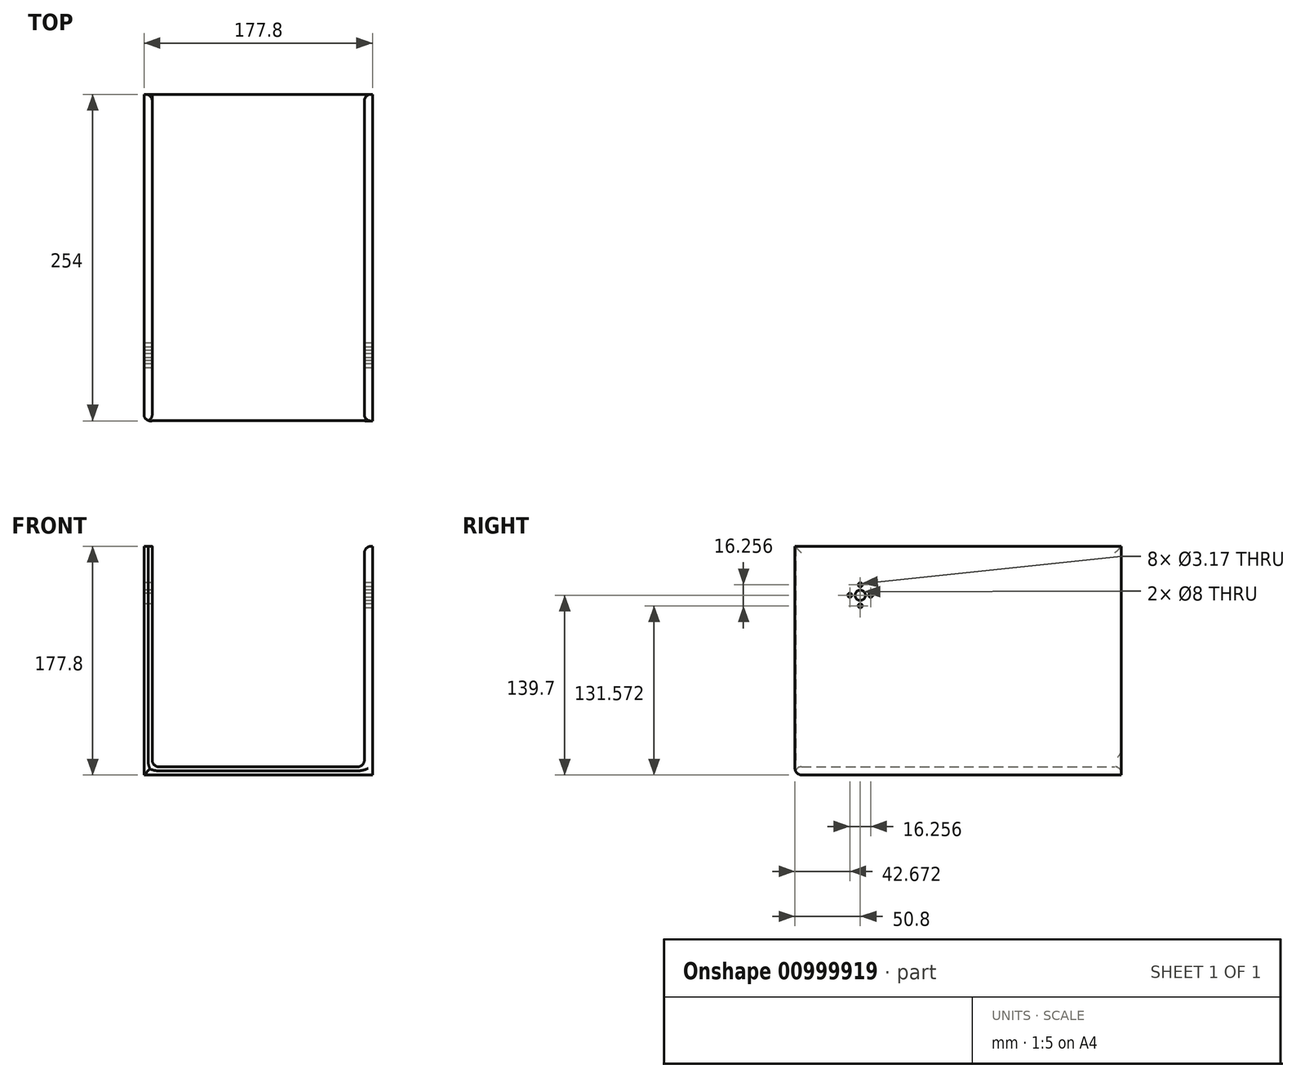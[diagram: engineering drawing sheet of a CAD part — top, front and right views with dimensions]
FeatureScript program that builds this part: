
annotation { "Feature Type Name" : "Feature", "Feature Type Description" : "" }
export const myFeature = defineFeature(function(context is Context, id is Id, definition is map)
    precondition{}
    {
        {
            var Q0;
            Q0=qCreatedBy(makeId("Front.planeOp"),FACE);
            var sketch = newSketch(context, id + "F0", { "sketchPlane" : qUnion([Q0])});
            skLineSegment(sketch, "E0.bottom", {"start": v(88.9, -88.9) * mm, "end": v(-88.9, -88.9) * mm});
            skLineSegment(sketch, "E0.top", {"start": v(88.9, 88.9) * mm, "end": v(82.55, 88.9) * mm});
            skLineSegment(sketch, "E0.left", {"start": v(88.9, -88.9) * mm, "end": v(88.9, 88.9) * mm});
            skLineSegment(sketch, "E0.right", {"start": v(-88.9, -88.9) * mm, "end": v(-88.9, 88.9) * mm});
            skPoint(sketch, "E0.middle", {"position": v(0, 0) * mm});
            skLineSegment(sketch, "E1.top", {"start": v(82.55, -82.55) * mm, "end": v(-82.55, -82.55) * mm});
            skPoint(sketch, "E1.right.start.orphan", {"position": v(-82.55, 82.55) * mm});
            skPoint(sketch, "E1.left.start.orphan", {"position": v(82.55, 82.55) * mm});
            skLineSegment(sketch, "E2", {"start": v(-82.55, -82.55) * mm, "end": v(-82.55, 88.9) * mm});
            skLineSegment(sketch, "E3", {"start": v(82.55, -82.55) * mm, "end": v(82.55, 88.9) * mm});
            skLineSegment(sketch, "E4.trimOffspring", {"start": v(-82.55, 88.9) * mm, "end": v(-88.9, 88.9) * mm});
            skSolve(sketch);
        }
        {
            var Q0;
            Q0=makeQuery(id+"F0.imprint","IMPRINT",FACE,{"disambiguationData":[TD([[makeQuery(id+"F0.imprint","IMPRINT",EDGE,{"derivedFrom":sQuery(id+"F0.wireOp",EDGE,"E0.bottom")}),-1.0]])]});
            extrude(context, id + "F1", {"entities" : qUnion([Q0]), "depth" : 254 * mm, "offsetDistance" : 25.4 * mm});
        }
        {
            var Q0;
            Q0=makeQuery(id+"F1.opExtrude","CAP_EDGE",EDGE,{"disambiguationData":[OSD([sQuery(id+"F0.wireOp",EDGE,"E0.bottom")])],"isStart":false});
            var Q1;
            Q1=makeQuery(id+"F1.opExtrude","CAP_EDGE",EDGE,{"disambiguationData":[OSD([sQuery(id+"F0.wireOp",EDGE,"E2")])],"isStart":false});
            var Q2;
            Q2=makeQuery(id+"F1.opExtrude","SWEPT_FACE",FACE,{"disambiguationData":[OSD([sQuery(id+"F0.wireOp",EDGE,"E3")])]});
            var Q3;
            Q3=makeQuery(id+"F1.opExtrude","SWEPT_FACE",FACE,{"disambiguationData":[OSD([sQuery(id+"F0.wireOp",EDGE,"E1.top")])]});
            var Q4;
            Q4=makeQuery(id+"F1.opExtrude","CAP_EDGE",EDGE,{"disambiguationData":[OSD([sQuery(id+"F0.wireOp",EDGE,"E0.right")])],"isStart":false});
            fillet(context, id + "F2", {"entities" : qUnion([Q0, Q1, Q2, Q3, Q4]), "tangentPropagation" : true, "radius" : 5.08 * mm, "defaultsChanged" : false, "vertexSettings" : [], "allowEdgeOverflow" : false});
        }
        {
            var Q0;
            Q0=makeQuery(id+"F1.opExtrude","SWEPT_FACE",FACE,{"disambiguationData":[OSD([sQuery(id+"F0.wireOp",EDGE,"E0.right")])]});
            var sketch = newSketch(context, id + "F3", { "sketchPlane" : qUnion([Q0])});
            skCircle(sketch, "E5", {"center": v(203.2, 50.8) * mm, "radius": 4 * mm});
            skCircle(sketch, "E6", {"center": v(195.07, 50.8) * mm, "radius": 1.59 * mm});
            skCircle(sketch, "E7", {"center": v(211.33, 50.8) * mm, "radius": 1.59 * mm});
            skCircle(sketch, "E8", {"center": v(203.2, 58.93) * mm, "radius": 1.59 * mm});
            skCircle(sketch, "E9", {"center": v(203.2, 42.67) * mm, "radius": 1.59 * mm});
            skSolve(sketch);
        }
        {
            var Q0;
            Q0=makeQuery(id+"F3.imprint","IMPRINT",FACE,{"disambiguationData":[TD([[makeQuery(id+"F3.imprint","IMPRINT",EDGE,{"derivedFrom":sQuery(id+"F3.wireOp",EDGE,"E5")}),1.0]])]});
            var Q1;
            Q1=makeQuery(id+"F3.imprint","IMPRINT",FACE,{"disambiguationData":[TD([[makeQuery(id+"F3.imprint","IMPRINT",EDGE,{"derivedFrom":sQuery(id+"F3.wireOp",EDGE,"E7")}),1.0]])]});
            var Q2;
            Q2=makeQuery(id+"F3.imprint","IMPRINT",FACE,{"disambiguationData":[TD([[makeQuery(id+"F3.imprint","IMPRINT",EDGE,{"derivedFrom":sQuery(id+"F3.wireOp",EDGE,"E9")}),1.0]])]});
            var Q3;
            Q3=makeQuery(id+"F3.imprint","IMPRINT",FACE,{"disambiguationData":[TD([[makeQuery(id+"F3.imprint","IMPRINT",EDGE,{"derivedFrom":sQuery(id+"F3.wireOp",EDGE,"E6")}),1.0]])]});
            var Q4;
            Q4=makeQuery(id+"F3.imprint","IMPRINT",FACE,{"disambiguationData":[TD([[makeQuery(id+"F3.imprint","IMPRINT",EDGE,{"derivedFrom":sQuery(id+"F3.wireOp",EDGE,"E8")}),1.0]])]});
            extrude(context, id + "F4", {"entities" : qUnion([Q0, Q1, Q2, Q3, Q4]), "operationType" : NewBodyOperationType.REMOVE, "oppositeDirection" : true, "depth" : 203.2 * mm, "offsetDistance" : 25.4 * mm});
        }
    });
